# Revit family: NLRS_57_AIR_UN_steel_wheather_wall_louvre_bmxn_exhaust_LT_sacs
name_source: partatom
category: Air Terminals
units: mm (PartAtom-declared; Revit-internal decimal feet)

## family parameters
Always vertical = No
Cut with Voids When Loaded = Yes
OmniClass Number = 23.75.70.21.27.11
OmniClass Title = Diffusers, Registers, and Grilles
Part Type = Normal
Room Calculation Point = Yes
Round Connector Dimension = Use Diameter
Shared = No
Work Plane-Based = No

## types (4) — shared parameters
Assembly Code = 57.0
Description = Solid Air weather louvre BMX (air exhaust)
FireRating = 0
IfcDescription = Solid Air weather louvre BMX (air exhaust)
IfcExportAs = IfcAirTerminal
IfcExportType = LOUVRE
IsExternal = No
LoadBearing = No
Manufacturer = Solid Air Climate Systems
Max Flow = 0.0 m³/h
Min Flow = 0.0 m³/h
Model = Weather louvre
NLRS_C_content_datum_uitgifte = 09-10-2025
NLRS_C_content_provider = Solid Air Climate Solutions
NLRS_C_content_versie = 4.22.01
NLRS_C_description = Solid Air weather louvre BMX (air exhaust)
SACS_Data_Hidden = BMX
URL = https://solid-air.nl
zero-valued in all types: Default Elevation

## per-type parameters (varying)
| type | SACS_Base_Index | SACS_Factor_NDF1 | SACS_Factor_NDF2 | SACS_Factor_NDF3 | SACS_Factor_NDF4 | SACS_Factor_NDF5 | SACS_Factor_NDF6 |
| BMXNGO | 1 | -0.364642 | -2261030.097 | 5342.127 | -665391.5911 | -59134.52062 | -10392644.78 |
| BMXNGI | 2 | -0.364642 | -2261030.097 | 5342.127 | -665391.5911 | -59134.52062 | -10392644.78 |
| BMXNSO | 3 | -0.415287 | -1695772.573 | 4006.5952 | -499043.6933 | -44350.89047 | -7794483.584 |
| BMXNSI | 4 | -0.415287 | -1695772.573 | 4006.5952 | -499043.6933 | -44350.89047 | -7794483.584 |

## geometry (parser evidence)
native form markers: Sweep x9
no freeform markers — native parametric forms only
